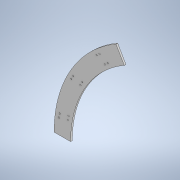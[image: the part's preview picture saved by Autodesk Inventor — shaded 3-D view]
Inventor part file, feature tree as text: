
AUTODESK INVENTOR PART (.ipt)
format: ipt  version: 2020.3 (Build 243373000, 373)  size: 141,824 bytes
history: native  units: mm
features: extrude x3, sketch x2, pattern_circular x1
ambient origin geometry x8: Origin, YZ Plane, XZ Plane, XY Plane, X Axis, Y Axis, Z Axis, Center Point
bodies: Solid1 (feature_tree)
feature tree (6):
  extrude  "Extrusion1"  Depth=40.0mm
  extrude  "Extrusion2"  Depth=10.0mm TaperAngle=0.0deg
  extrude  "Extrusion3"  Depth=10.0mm
  pattern_circular  "Circular Pattern1"  [2 undecoded]
  sketch  "Sketch1"  dims[d0=600.0mm d1=40.0mm]
  sketch  "Sketch3"  dims[d2=4.0mm d3=0.0mm d4=10.0mm d5=0.0mm d6=3.0mm d7=3.0mm d9=270.0mm d11=3.0mm d12=3.0mm d14=270.0mm d16=0.0mm d17=0.0mm d18=90.0mm d19=27.925268mm d21=20.071286mm d22=20.0mm d23=1.570796mm d24=1.919862mm d25=60.0deg]
note: 2 required parameter values undecoded (feature->parameter linkage not recoverable at this tier; creation-order binding heuristic only, values carry confidence <= 0.55)
